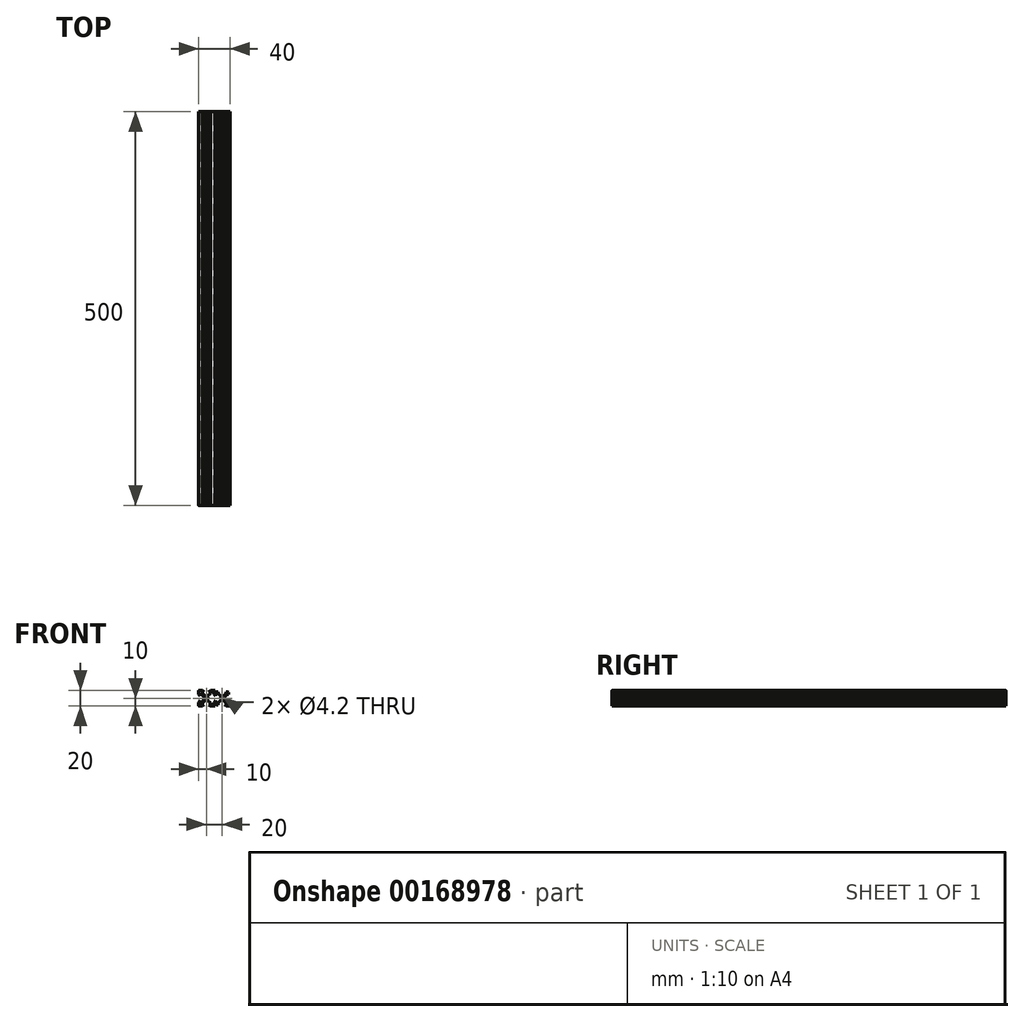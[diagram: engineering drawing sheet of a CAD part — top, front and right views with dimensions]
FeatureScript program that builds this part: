
annotation { "Feature Type Name" : "Feature", "Feature Type Description" : "" }
export const myFeature = defineFeature(function(context is Context, id is Id, definition is map)
    precondition{}
    {
        {
            var Q0;
            Q0=qCreatedBy(makeId("Front.planeOp"),FACE);
            var sketch = newSketch(context, id + "F0", { "sketchPlane" : qUnion([Q0])});
            skLineSegment(sketch, "E0.left", {"start": v(15, 1) * mm, "end": v(15, 4.89) * mm});
            skLineSegment(sketch, "E0.right", {"start": v(35, 1) * mm, "end": v(35, 4.89) * mm});
            skLineSegment(sketch, "E1.right", {"start": v(33.2, 2.97) * mm, "end": v(33.2, 7.06) * mm});
            skLineSegment(sketch, "E2.rect.bottom", {"start": v(26.78, 12.84) * mm, "end": v(23.22, 12.84) * mm});
            skLineSegment(sketch, "E2.rect.top", {"start": v(26.78, 7.16) * mm, "end": v(23.31, 7.16) * mm});
            skLineSegment(sketch, "E2.rect.left", {"start": v(27.84, 11.78) * mm, "end": v(27.84, 8.33) * mm});
            skLineSegment(sketch, "E2.rect.right", {"start": v(22.16, 11.78) * mm, "end": v(22.16, 8.22) * mm});
            skLineSegment(sketch, "E3.rect.bottom", {"start": v(35, 15.12) * mm, "end": v(35, 15.12) * mm});
            skLineSegment(sketch, "E4.rect.bottom", {"start": v(33.2, 12.95) * mm, "end": v(33.2, 12.95) * mm});
            skPoint(sketch, "E4.rect.middle", {"position": v(33.2, 10) * mm});
            skLineSegment(sketch, "E5", {"start": v(35, 4.88) * mm, "end": v(33.2, 7.05) * mm});
            skLineSegment(sketch, "E6", {"start": v(28.37, 12.3) * mm, "end": v(33.2, 17.14) * mm});
            skLineSegment(sketch, "E7", {"start": v(27.3, 13.37) * mm, "end": v(32.14, 18.2) * mm});
            skLineSegment(sketch, "E8", {"start": v(22.7, 13.37) * mm, "end": v(17.86, 18.2) * mm});
            skLineSegment(sketch, "E9", {"start": v(28.37, 7.8) * mm, "end": v(33.2, 2.97) * mm});
            skLineSegment(sketch, "E10", {"start": v(22.74, 6.58) * mm, "end": v(17.95, 1.8) * mm});
            skLineSegment(sketch, "E11", {"start": v(27.36, 6.58) * mm, "end": v(32.14, 1.8) * mm});
            skLineSegment(sketch, "E12", {"start": v(21.63, 7.7) * mm, "end": v(16.8, 2.86) * mm});
            skLineSegment(sketch, "E13", {"start": v(22.7, 13.37) * mm, "end": v(23.22, 12.84) * mm});
            skLineSegment(sketch, "E14", {"start": v(27.3, 13.37) * mm, "end": v(26.78, 12.84) * mm});
            skLineSegment(sketch, "E15", {"start": v(28.37, 12.3) * mm, "end": v(27.84, 11.78) * mm});
            skLineSegment(sketch, "E16", {"start": v(28.37, 7.8) * mm, "end": v(27.84, 8.33) * mm});
            skLineSegment(sketch, "E17", {"start": v(27.36, 6.58) * mm, "end": v(26.78, 7.16) * mm});
            skLineSegment(sketch, "E18", {"start": v(22.74, 6.58) * mm, "end": v(23.31, 7.16) * mm});
            skLineSegment(sketch, "E19", {"start": v(21.63, 7.7) * mm, "end": v(22.16, 8.22) * mm});
            skLineSegment(sketch, "E20", {"start": v(21.63, 12.3) * mm, "end": v(16.8, 17.14) * mm});
            skLineSegment(sketch, "E21", {"start": v(21.63, 12.3) * mm, "end": v(22.16, 11.78) * mm});
            skPoint(sketch, "E22.orphan", {"position": v(22.16, 12.84) * mm});
            skPoint(sketch, "E23.orphan", {"position": v(27.84, 12.84) * mm});
            skPoint(sketch, "E24.orphan", {"position": v(27.84, 7.16) * mm});
            skPoint(sketch, "E25.orphan", {"position": v(22.16, 7.16) * mm});
            skPoint(sketch, "E26.orphan", {"position": v(33.2, 18.2) * mm});
            skPoint(sketch, "E27.orphan", {"position": v(33.2, 1.8) * mm});
            skLineSegment(sketch, "E28.trimOffspring", {"start": v(35, 15.12) * mm, "end": v(35, 19) * mm});
            skLineSegment(sketch, "E29.rect.left", {"start": v(28.21, 18.2) * mm, "end": v(28.21, 18.2) * mm});
            skLineSegment(sketch, "E29.rect.right", {"start": v(21.79, 18.2) * mm, "end": v(21.79, 18.2) * mm});
            skLineSegment(sketch, "E30.rect.left", {"start": v(27.72, 16.15) * mm, "end": v(27.72, 16.15) * mm});
            skLineSegment(sketch, "E30.rect.right", {"start": v(21.83, 16.15) * mm, "end": v(21.83, 16.15) * mm});
            skLineSegment(sketch, "E31.trimOffspring", {"start": v(15, 15.12) * mm, "end": v(15, 19) * mm});
            skPoint(sketch, "E32.visualSharp", {"position": v(15, 20) * mm});
            skArc(sketch, "E32.filletArc", {"start": v(16, 20) * mm, "mid": v(15.3, 19.7) * mm, "end": v(15, 19) * mm});
            skArc(sketch, "E33.filletArc", {"start": v(34, 0) * mm, "mid": v(34.7, 0.3) * mm, "end": v(35, 1) * mm});
            skPoint(sketch, "E34.visualSharp", {"position": v(35, 20) * mm});
            skArc(sketch, "E34.filletArc", {"start": v(35, 19) * mm, "mid": v(34.7, 19.7) * mm, "end": v(34, 20) * mm});
            skLineSegment(sketch, "E35", {"start": v(17.95, 1.8) * mm, "end": v(17.95, 0) * mm});
            skArc(sketch, "E36.filletArc", {"start": v(15, 1) * mm, "mid": v(15.3, 0.3) * mm, "end": v(16, 0) * mm});
            skLineSegment(sketch, "E37", {"start": v(16.8, 17.14) * mm, "end": v(17.86, 18.2) * mm});
            skPoint(sketch, "E38.visualSharp", {"position": v(16.8, 12.95) * mm});
            skLineSegment(sketch, "E39", {"start": v(16.8, 2.86) * mm, "end": v(17.95, 1.8) * mm});
            skLineSegment(sketch, "E40", {"start": v(32.14, 1.8) * mm, "end": v(33.2, 2.97) * mm});
            skLineSegment(sketch, "E41", {"start": v(32.14, 18.2) * mm, "end": v(33.2, 17.14) * mm});
            skLineSegment(sketch, "E42", {"start": v(33.2, 17.14) * mm, "end": v(33.2, 12.94) * mm});
            skLineSegment(sketch, "E43", {"start": v(35, 15.12) * mm, "end": v(33.2, 12.95) * mm});
            skPoint(sketch, "E44.visualSharp", {"position": v(16.8, 7.06) * mm});
            skLineSegment(sketch, "E45", {"start": v(33.2, 15.12) * mm, "end": v(31.18, 15.12) * mm});
            skLineSegment(sketch, "E46", {"start": v(16.8, 15.12) * mm, "end": v(18.82, 15.12) * mm});
            skLineSegment(sketch, "E47", {"start": v(16.8, 4.89) * mm, "end": v(18.82, 4.89) * mm});
            skLineSegment(sketch, "E48", {"start": v(33.2, 4.89) * mm, "end": v(31.28, 4.88) * mm});
            skLineSegment(sketch, "E49.rect.left", {"start": v(26.7, 18.2) * mm, "end": v(26.7, 18.2) * mm});
            skLineSegment(sketch, "E49.rect.right", {"start": v(23.3, 18.2) * mm, "end": v(23.3, 18.2) * mm});
            skPoint(sketch, "E49.rect.middle", {"position": v(25, 18.2) * mm});
            skLineSegment(sketch, "E50.rect.left", {"start": v(30.11, 20) * mm, "end": v(30.11, 20) * mm});
            skLineSegment(sketch, "E50.rect.right", {"start": v(19.88, 20) * mm, "end": v(19.88, 20) * mm});
            skPoint(sketch, "E50.rect.middle", {"position": v(25, 20) * mm});
            skLineSegment(sketch, "E51.rect.left", {"start": v(27.95, 18.2) * mm, "end": v(27.95, 18.2) * mm});
            skLineSegment(sketch, "E51.rect.right", {"start": v(22.05, 18.2) * mm, "end": v(22.05, 18.2) * mm});
            skLineSegment(sketch, "E52", {"start": v(22.05, 18.2) * mm, "end": v(19.88, 20) * mm});
            skLineSegment(sketch, "E53", {"start": v(27.94, 18.2) * mm, "end": v(30.11, 20) * mm});
            skLineSegment(sketch, "E54", {"start": v(27.94, 18.2) * mm, "end": v(32.14, 18.2) * mm});
            skLineSegment(sketch, "E55", {"start": v(30.11, 20) * mm, "end": v(34, 20) * mm});
            skLineSegment(sketch, "E56", {"start": v(19.88, 20) * mm, "end": v(16, 20) * mm});
            skLineSegment(sketch, "E57", {"start": v(17.86, 18.2) * mm, "end": v(22.05, 18.2) * mm});
            skLineSegment(sketch, "E58", {"start": v(15, 15.11) * mm, "end": v(16.8, 12.94) * mm});
            skLineSegment(sketch, "E59", {"start": v(16.8, 17.14) * mm, "end": v(16.8, 12.95) * mm});
            skLineSegment(sketch, "E60", {"start": v(15, 4.89) * mm, "end": v(16.8, 7.06) * mm});
            skLineSegment(sketch, "E61", {"start": v(16.8, 2.86) * mm, "end": v(16.8, 7.06) * mm});
            skLineSegment(sketch, "E62", {"start": v(22.05, 1.8) * mm, "end": v(19.88, 0) * mm});
            skLineSegment(sketch, "E63", {"start": v(27.94, 1.8) * mm, "end": v(30.11, 0) * mm});
            skLineSegment(sketch, "E64", {"start": v(16, 0) * mm, "end": v(19.88, 0) * mm});
            skLineSegment(sketch, "E65", {"start": v(30.11, 0) * mm, "end": v(34, 0) * mm});
            skLineSegment(sketch, "E66", {"start": v(27.94, 1.8) * mm, "end": v(32.14, 1.8) * mm});
            skLineSegment(sketch, "E67", {"start": v(22.05, 1.8) * mm, "end": v(17.95, 1.8) * mm});
            skLineSegment(sketch, "E68", {"start": v(19.88, 1.8) * mm, "end": v(19.88, 3.73) * mm});
            skLineSegment(sketch, "E69", {"start": v(30.11, 1.8) * mm, "end": v(30.11, 3.83) * mm});
            skLineSegment(sketch, "E70", {"start": v(30.11, 18.2) * mm, "end": v(30.11, 16.18) * mm});
            skLineSegment(sketch, "E71", {"start": v(19.88, 16.18) * mm, "end": v(19.88, 18.2) * mm});
            skLineSegment(sketch, "E72", {"start": v(15, 0) * mm, "end": v(-35, 0) * mm});
            skLineSegment(sketch, "E73", {"start": v(35, 0) * mm, "end": v(35, 20) * mm});
            skLineSegment(sketch, "E74", {"start": v(34, 0) * mm, "end": v(35, 0) * mm});
            skLineSegment(sketch, "E75", {"start": v(34, 20) * mm, "end": v(35, 20) * mm});
            skLineSegment(sketch, "E76.0.MirrorCS", {"start": v(36, 0) * mm, "end": v(35, 0) * mm});
            skArc(sketch, "E76.1.MirrorCS", {"start": v(36, 0) * mm, "mid": v(35.3, 0.3) * mm, "end": v(35, 1) * mm});
            skLineSegment(sketch, "E76.2.MirrorCS", {"start": v(36, 20) * mm, "end": v(35, 20) * mm});
            skLineSegment(sketch, "E76.3.MirrorCS", {"start": v(54, 0) * mm, "end": v(50.12, 0) * mm});
            skLineSegment(sketch, "E76.4.MirrorCS", {"start": v(48.37, 7.7) * mm, "end": v(47.84, 8.22) * mm});
            skArc(sketch, "E76.5.MirrorCS", {"start": v(35, 19) * mm, "mid": v(35.3, 19.7) * mm, "end": v(36, 20) * mm});
            skLineSegment(sketch, "E76.6.MirrorCS", {"start": v(37.86, 1.8) * mm, "end": v(36.8, 2.97) * mm});
            skArc(sketch, "E76.7.MirrorCS", {"start": v(54, 20) * mm, "mid": v(54.7, 19.7) * mm, "end": v(55, 19) * mm});
            skLineSegment(sketch, "E76.8.MirrorCS", {"start": v(42.64, 6.58) * mm, "end": v(43.22, 7.16) * mm});
            skLineSegment(sketch, "E76.9.MirrorCS", {"start": v(41.63, 7.8) * mm, "end": v(42.16, 8.33) * mm});
            skLineSegment(sketch, "E76.10.MirrorCS", {"start": v(37.86, 18.2) * mm, "end": v(36.8, 17.14) * mm});
            skLineSegment(sketch, "E76.11.MirrorCS", {"start": v(42.7, 13.37) * mm, "end": v(43.22, 12.84) * mm});
            skLineSegment(sketch, "E76.12.MirrorCS", {"start": v(53.2, 2.86) * mm, "end": v(52.05, 1.8) * mm});
            skLineSegment(sketch, "E76.13.MirrorCS", {"start": v(53.2, 17.14) * mm, "end": v(52.14, 18.2) * mm});
            skLineSegment(sketch, "E76.14.MirrorCS", {"start": v(48.37, 12.3) * mm, "end": v(47.84, 11.78) * mm});
            skLineSegment(sketch, "E76.15.MirrorCS", {"start": v(47.3, 13.37) * mm, "end": v(46.78, 12.84) * mm});
            skLineSegment(sketch, "E76.16.MirrorCS", {"start": v(47.26, 6.58) * mm, "end": v(46.69, 7.16) * mm});
            skLineSegment(sketch, "E76.17.MirrorCS", {"start": v(36.8, 15.12) * mm, "end": v(38.82, 15.12) * mm});
            skLineSegment(sketch, "E76.19.MirrorCS", {"start": v(54, 0) * mm, "end": v(50.12, 0) * mm});
            skLineSegment(sketch, "E76.20.MirrorCS", {"start": v(36.8, 4.89) * mm, "end": v(38.72, 4.88) * mm});
            skArc(sketch, "E76.21.MirrorCS", {"start": v(55, 1) * mm, "mid": v(54.7, 0.3) * mm, "end": v(54, 0) * mm});
            skLineSegment(sketch, "E76.22.MirrorCS", {"start": v(55, 4.89) * mm, "end": v(53.2, 7.06) * mm});
            skLineSegment(sketch, "E76.23.MirrorCS", {"start": v(52.14, 18.2) * mm, "end": v(47.95, 18.2) * mm});
            skLineSegment(sketch, "E76.25.MirrorCS", {"start": v(47.95, 18.2) * mm, "end": v(50.12, 20) * mm});
            skLineSegment(sketch, "E76.26.MirrorCS", {"start": v(50.12, 1.8) * mm, "end": v(50.12, 3.73) * mm});
            skLineSegment(sketch, "E76.27.MirrorCS", {"start": v(39.89, 0) * mm, "end": v(36, 0) * mm});
            skLineSegment(sketch, "E76.28.MirrorCS", {"start": v(53.2, 15.12) * mm, "end": v(51.18, 15.12) * mm});
            skPoint(sketch, "E76.29.MirrorP", {"position": v(45, 18.2) * mm});
            skLineSegment(sketch, "E76.30.MirrorCS", {"start": v(48.21, 18.2) * mm, "end": v(48.21, 18.2) * mm});
            skLineSegment(sketch, "E76.31.MirrorCS", {"start": v(42.06, 18.2) * mm, "end": v(39.89, 20) * mm});
            skLineSegment(sketch, "E76.32.MirrorCS", {"start": v(41.63, 12.3) * mm, "end": v(42.16, 11.78) * mm});
            skLineSegment(sketch, "E76.33.MirrorCS", {"start": v(41.79, 18.2) * mm, "end": v(41.79, 18.2) * mm});
            skLineSegment(sketch, "E76.34.MirrorCS", {"start": v(36.8, 17.14) * mm, "end": v(36.8, 12.94) * mm});
            skLineSegment(sketch, "E76.35.MirrorCS", {"start": v(50.12, 16.18) * mm, "end": v(50.12, 18.2) * mm});
            skLineSegment(sketch, "E76.36.MirrorCS", {"start": v(42.06, 1.8) * mm, "end": v(39.89, 0) * mm});
            skLineSegment(sketch, "E76.37.MirrorCS", {"start": v(35, 15.12) * mm, "end": v(36.8, 12.95) * mm});
            skLineSegment(sketch, "E76.38.MirrorCS", {"start": v(35, 4.88) * mm, "end": v(36.8, 7.05) * mm});
            skLineSegment(sketch, "E76.39.MirrorCS", {"start": v(53.2, 17.14) * mm, "end": v(53.2, 12.95) * mm});
            skLineSegment(sketch, "E76.40.MirrorCS", {"start": v(55, 15.12) * mm, "end": v(53.2, 12.94) * mm});
            skLineSegment(sketch, "E76.41.MirrorCS", {"start": v(53.2, 4.89) * mm, "end": v(51.18, 4.89) * mm});
            skLineSegment(sketch, "E76.42.MirrorCS", {"start": v(36.8, 2.97) * mm, "end": v(36.8, 7.06) * mm});
            skLineSegment(sketch, "E76.43.MirrorCS", {"start": v(39.89, 18.2) * mm, "end": v(39.89, 16.18) * mm});
            skLineSegment(sketch, "E76.44.MirrorCS", {"start": v(42.06, 18.2) * mm, "end": v(37.86, 18.2) * mm});
            skLineSegment(sketch, "E76.45.MirrorCS", {"start": v(53.2, 2.86) * mm, "end": v(53.2, 7.06) * mm});
            skLineSegment(sketch, "E76.46.MirrorCS", {"start": v(42.06, 1.8) * mm, "end": v(37.86, 1.8) * mm});
            skLineSegment(sketch, "E76.47.MirrorCS", {"start": v(52.05, 1.8) * mm, "end": v(52.05, 0) * mm});
            skLineSegment(sketch, "E76.48.MirrorCS", {"start": v(39.89, 1.8) * mm, "end": v(39.89, 3.83) * mm});
            skPoint(sketch, "E76.49.MirrorP", {"position": v(55, 20) * mm});
            skLineSegment(sketch, "E76.50.MirrorCS", {"start": v(47.95, 1.8) * mm, "end": v(52.05, 1.8) * mm});
            skLineSegment(sketch, "E76.51.MirrorCS", {"start": v(41.63, 7.8) * mm, "end": v(36.8, 2.97) * mm});
            skPoint(sketch, "E76.52.MirrorP", {"position": v(53.2, 7.06) * mm});
            skLineSegment(sketch, "E76.53.MirrorCS", {"start": v(43.22, 7.16) * mm, "end": v(46.69, 7.16) * mm});
            skLineSegment(sketch, "E76.54.MirrorCS", {"start": v(55, 1) * mm, "end": v(55, 4.89) * mm});
            skLineSegment(sketch, "E76.55.MirrorCS", {"start": v(55, 15.12) * mm, "end": v(55, 19) * mm});
            skLineSegment(sketch, "E76.56.MirrorCS", {"start": v(48.37, 12.3) * mm, "end": v(53.2, 17.14) * mm});
            skLineSegment(sketch, "E76.57.MirrorCS", {"start": v(42.28, 16.15) * mm, "end": v(42.28, 16.15) * mm});
            skLineSegment(sketch, "E76.58.MirrorCS", {"start": v(36.8, 12.95) * mm, "end": v(36.8, 12.95) * mm});
            skLineSegment(sketch, "E76.60.MirrorCS", {"start": v(42.05, 18.2) * mm, "end": v(42.05, 18.2) * mm});
            skLineSegment(sketch, "E76.61.MirrorCS", {"start": v(47.26, 6.58) * mm, "end": v(52.05, 1.8) * mm});
            skLineSegment(sketch, "E76.62.MirrorCS", {"start": v(42.7, 13.37) * mm, "end": v(37.86, 18.2) * mm});
            skPoint(sketch, "E76.63.MirrorP", {"position": v(42.16, 12.84) * mm});
            skLineSegment(sketch, "E76.64.MirrorCS", {"start": v(48.17, 16.15) * mm, "end": v(48.17, 16.15) * mm});
            skLineSegment(sketch, "E76.65.MirrorCS", {"start": v(42.16, 11.78) * mm, "end": v(42.16, 8.33) * mm});
            skLineSegment(sketch, "E76.66.MirrorCS", {"start": v(47.84, 11.78) * mm, "end": v(47.84, 8.22) * mm});
            skLineSegment(sketch, "E76.67.MirrorCS", {"start": v(43.22, 12.84) * mm, "end": v(46.78, 12.84) * mm});
            skPoint(sketch, "E76.68.MirrorP", {"position": v(36.8, 18.2) * mm});
            skPoint(sketch, "E76.69.MirrorP", {"position": v(53.2, 12.95) * mm});
            skLineSegment(sketch, "E76.72.MirrorCS", {"start": v(39.89, 20) * mm, "end": v(36, 20) * mm});
            skPoint(sketch, "E76.73.MirrorP", {"position": v(42.16, 7.16) * mm});
            skLineSegment(sketch, "E76.74.MirrorCS", {"start": v(47.3, 13.37) * mm, "end": v(52.14, 18.2) * mm});
            skLineSegment(sketch, "E76.75.MirrorCS", {"start": v(43.3, 18.2) * mm, "end": v(43.3, 18.2) * mm});
            skLineSegment(sketch, "E76.76.MirrorCS", {"start": v(39.89, 0) * mm, "end": v(36, 0) * mm});
            skLineSegment(sketch, "E76.77.MirrorCS", {"start": v(54, 0) * mm, "end": v(50.12, 0) * mm});
            skLineSegment(sketch, "E76.78.MirrorCS", {"start": v(39.89, 0) * mm, "end": v(36, 0) * mm});
            skPoint(sketch, "E76.79.MirrorP", {"position": v(45, 20) * mm});
            skPoint(sketch, "E76.80.MirrorP", {"position": v(47.84, 7.16) * mm});
            skLineSegment(sketch, "E76.81.MirrorCS", {"start": v(39.89, 20) * mm, "end": v(39.89, 20) * mm});
            skLineSegment(sketch, "E76.82.MirrorCS", {"start": v(47.95, 18.2) * mm, "end": v(47.95, 18.2) * mm});
            skLineSegment(sketch, "E76.83.MirrorCS", {"start": v(50.12, 20) * mm, "end": v(50.12, 20) * mm});
            skLineSegment(sketch, "E76.84.MirrorCS", {"start": v(41.63, 12.3) * mm, "end": v(36.8, 17.14) * mm});
            skLineSegment(sketch, "E76.85.MirrorCS", {"start": v(48.37, 7.7) * mm, "end": v(53.2, 2.86) * mm});
            skPoint(sketch, "E76.86.MirrorP", {"position": v(36.8, 1.8) * mm});
            skPoint(sketch, "E76.87.MirrorP", {"position": v(36.8, 10) * mm});
            skPoint(sketch, "E76.88.MirrorP", {"position": v(45, 18.2) * mm});
            skPoint(sketch, "E76.89.MirrorP", {"position": v(47.84, 12.84) * mm});
            skLineSegment(sketch, "E76.90.MirrorCS", {"start": v(47.95, 1.8) * mm, "end": v(50.12, 0) * mm});
            skLineSegment(sketch, "E76.91.MirrorCS", {"start": v(42.64, 6.58) * mm, "end": v(37.86, 1.8) * mm});
            skLineSegment(sketch, "E76.94.MirrorCS", {"start": v(50.12, 20) * mm, "end": v(54, 20) * mm});
            skLineSegment(sketch, "E76.95.MirrorCS", {"start": v(46.7, 18.2) * mm, "end": v(46.7, 18.2) * mm});
            skSolve(sketch);
        }
        {
            var Q0;
            {var subQ1=sQuery(id+"F0.wireOp",EDGE,"E76.41.MirrorCS");Q0=makeQuery(id+"F0.imprint","IMPRINT",FACE,{"disambiguationData":[TD([[makeQuery(id+"F0.imprint","IMPRINT",EDGE,{"derivedFrom":subQ1}),1.0]])]});}
            var Q1;
            Q1=makeQuery(id+"F0.imprint","IMPRINT",FACE,{"disambiguationData":[TD([[makeQuery(id+"F0.imprint","IMPRINT",EDGE,{"derivedFrom":sQuery(id+"F0.wireOp",EDGE,"E76.1.MirrorCS")}),-1.0]])]});
            var Q2;
            {var subQ4=sQuery(id+"F0.wireOp",EDGE,"E5");Q2=makeQuery(id+"F0.imprint","IMPRINT",FACE,{"disambiguationData":[TD([[makeQuery(id+"F0.imprint","IMPRINT",EDGE,{"derivedFrom":subQ4}),1.0]])]});}
            var Q3;
            Q3=makeQuery(id+"F0.imprint","IMPRINT",FACE,{"disambiguationData":[TD([[makeQuery(id+"F0.imprint","IMPRINT",EDGE,{"derivedFrom":sQuery(id+"F0.wireOp",EDGE,"E0.left")}),-1.0]])]});
            var Q4;
            {var subQ6=sQuery(id+"F0.wireOp",EDGE,"E76.12.MirrorCS");Q4=makeQuery(id+"F0.imprint","IMPRINT",FACE,{"disambiguationData":[TD([[makeQuery(id+"F0.imprint","IMPRINT",EDGE,{"derivedFrom":subQ6}),1.0]])]});}
            var Q5;
            {var subQ2=sQuery(id+"F0.wireOp",EDGE,"E76.47.MirrorCS");Q5=makeQuery(id+"F0.imprint","IMPRINT",FACE,{"disambiguationData":[TD([[makeQuery(id+"F0.imprint","IMPRINT",EDGE,{"derivedFrom":subQ2}),-1.0]])]});}
            var Q6;
            {var subQ6=sQuery(id+"F0.wireOp",EDGE,"E76.4.MirrorCS");Q6=makeQuery(id+"F0.imprint","IMPRINT",FACE,{"disambiguationData":[TD([[makeQuery(id+"F0.imprint","IMPRINT",EDGE,{"derivedFrom":subQ6}),1.0]])]});}
            var Q7;
            {var subQ2=sQuery(id+"F0.wireOp",EDGE,"E35");Q7=makeQuery(id+"F0.imprint","IMPRINT",FACE,{"disambiguationData":[TD([[makeQuery(id+"F0.imprint","IMPRINT",EDGE,{"derivedFrom":subQ2}),1.0]])]});}
            var Q8;
            Q8=makeQuery(id+"F0.imprint","IMPRINT",FACE,{"disambiguationData":[TD([[makeQuery(id+"F0.imprint","IMPRINT",EDGE,{"derivedFrom":sQuery(id+"F0.wireOp",EDGE,"E76.5.MirrorCS")}),-1.0]])]});
            var Q9;
            Q9=makeQuery(id+"F0.imprint","IMPRINT",FACE,{"disambiguationData":[TD([[makeQuery(id+"F0.imprint","IMPRINT",EDGE,{"derivedFrom":sQuery(id+"F0.wireOp",EDGE,"E31.trimOffspring")}),-1.0]])]});
            var Q10;
            {var subQ1=sQuery(id+"F0.wireOp",EDGE,"E76.17.MirrorCS");Q10=makeQuery(id+"F0.imprint","IMPRINT",FACE,{"disambiguationData":[TD([[makeQuery(id+"F0.imprint","IMPRINT",EDGE,{"derivedFrom":subQ1}),1.0]])]});}
            var Q11;
            {var subQ1=sQuery(id+"F0.wireOp",EDGE,"E76.35.MirrorCS");Q11=makeQuery(id+"F0.imprint","IMPRINT",FACE,{"disambiguationData":[TD([[makeQuery(id+"F0.imprint","IMPRINT",EDGE,{"derivedFrom":subQ1}),-1.0]])]});}
            var Q12;
            Q12=makeQuery(id+"F0.imprint","IMPRINT",FACE,{"disambiguationData":[TD([[makeQuery(id+"F0.imprint","IMPRINT",EDGE,{"derivedFrom":sQuery(id+"F0.wireOp",EDGE,"E34.filletArc")}),1.0]])]});
            var Q13;
            {var subQ5=sQuery(id+"F0.wireOp",EDGE,"E76.9.MirrorCS");Q13=makeQuery(id+"F0.imprint","IMPRINT",FACE,{"disambiguationData":[TD([[makeQuery(id+"F0.imprint","IMPRINT",EDGE,{"derivedFrom":subQ5}),1.0]])]});}
            var Q14;
            Q14=makeQuery(id+"F0.imprint","IMPRINT",FACE,{"disambiguationData":[TD([[makeQuery(id+"F0.imprint","IMPRINT",EDGE,{"derivedFrom":sQuery(id+"F0.wireOp",EDGE,"E76.7.MirrorCS")}),-1.0]])]});
            var Q15;
            Q15=makeQuery(id+"F0.imprint","IMPRINT",FACE,{"disambiguationData":[TD([[makeQuery(id+"F0.imprint","IMPRINT",EDGE,{"derivedFrom":sQuery(id+"F0.wireOp",EDGE,"E2.rect.bottom")}),1.0]])]});
            var Q16;
            {var subQ0=sQuery(id+"F0.wireOp",EDGE,"E70");Q16=makeQuery(id+"F0.imprint","IMPRINT",FACE,{"disambiguationData":[TD([[makeQuery(id+"F0.imprint","IMPRINT",EDGE,{"derivedFrom":subQ0}),1.0]])]});}
            var Q17;
            {var subQ1=sQuery(id+"F0.wireOp",EDGE,"E76.28.MirrorCS");Q17=makeQuery(id+"F0.imprint","IMPRINT",FACE,{"disambiguationData":[TD([[makeQuery(id+"F0.imprint","IMPRINT",EDGE,{"derivedFrom":subQ1}),-1.0]])]});}
            var Q18;
            Q18=makeQuery(id+"F0.imprint","IMPRINT",FACE,{"disambiguationData":[TD([[makeQuery(id+"F0.imprint","IMPRINT",EDGE,{"derivedFrom":sQuery(id+"F0.wireOp",EDGE,"E2.rect.left")}),1.0]])]});
            var Q19;
            {var subQ1=sQuery(id+"F0.wireOp",EDGE,"E71");Q19=makeQuery(id+"F0.imprint","IMPRINT",FACE,{"disambiguationData":[TD([[makeQuery(id+"F0.imprint","IMPRINT",EDGE,{"derivedFrom":subQ1}),1.0]])]});}
            var Q20;
            {var subQ1=sQuery(id+"F0.wireOp",EDGE,"E47");Q20=makeQuery(id+"F0.imprint","IMPRINT",FACE,{"disambiguationData":[TD([[makeQuery(id+"F0.imprint","IMPRINT",EDGE,{"derivedFrom":subQ1}),-1.0]])]});}
            var Q21;
            {var subQ0=sQuery(id+"F0.wireOp",EDGE,"E69");Q21=makeQuery(id+"F0.imprint","IMPRINT",FACE,{"disambiguationData":[TD([[makeQuery(id+"F0.imprint","IMPRINT",EDGE,{"derivedFrom":subQ0}),-1.0]])]});}
            var Q22;
            {var subQ1=sQuery(id+"F0.wireOp",EDGE,"E76.48.MirrorCS");Q22=makeQuery(id+"F0.imprint","IMPRINT",FACE,{"disambiguationData":[TD([[makeQuery(id+"F0.imprint","IMPRINT",EDGE,{"derivedFrom":subQ1}),1.0]])]});}
            var Q23;
            {var subQ1=sQuery(id+"F0.wireOp",EDGE,"E46");Q23=makeQuery(id+"F0.imprint","IMPRINT",FACE,{"disambiguationData":[TD([[makeQuery(id+"F0.imprint","IMPRINT",EDGE,{"derivedFrom":subQ1}),1.0]])]});}
            var Q24;
            {var subQ1=sQuery(id+"F0.wireOp",EDGE,"E76.26.MirrorCS");Q24=makeQuery(id+"F0.imprint","IMPRINT",FACE,{"disambiguationData":[TD([[makeQuery(id+"F0.imprint","IMPRINT",EDGE,{"derivedFrom":subQ1}),-1.0]])]});}
            var Q25;
            {var subQ1=sQuery(id+"F0.wireOp",EDGE,"E76.43.MirrorCS");Q25=makeQuery(id+"F0.imprint","IMPRINT",FACE,{"disambiguationData":[TD([[makeQuery(id+"F0.imprint","IMPRINT",EDGE,{"derivedFrom":subQ1}),-1.0]])]});}
            var Q26;
            {var subQ0=sQuery(id+"F0.wireOp",EDGE,"E48");Q26=makeQuery(id+"F0.imprint","IMPRINT",FACE,{"disambiguationData":[TD([[makeQuery(id+"F0.imprint","IMPRINT",EDGE,{"derivedFrom":subQ0}),1.0]])]});}
            var Q27;
            {var subQ0=sQuery(id+"F0.wireOp",EDGE,"E45");Q27=makeQuery(id+"F0.imprint","IMPRINT",FACE,{"disambiguationData":[TD([[makeQuery(id+"F0.imprint","IMPRINT",EDGE,{"derivedFrom":subQ0}),-1.0]])]});}
            var Q28;
            {var subQ1=sQuery(id+"F0.wireOp",EDGE,"E76.20.MirrorCS");Q28=makeQuery(id+"F0.imprint","IMPRINT",FACE,{"disambiguationData":[TD([[makeQuery(id+"F0.imprint","IMPRINT",EDGE,{"derivedFrom":subQ1}),-1.0]])]});}
            var Q29;
            {var subQ0=sQuery(id+"F0.wireOp",EDGE,"E68");Q29=makeQuery(id+"F0.imprint","IMPRINT",FACE,{"disambiguationData":[TD([[makeQuery(id+"F0.imprint","IMPRINT",EDGE,{"derivedFrom":subQ0}),1.0]])]});}
            var Q30;
            {var subQ1=sQuery(id+"F0.wireOp",EDGE,"E76.2.MirrorCS");Q30=makeQuery(id+"F0.imprint","IMPRINT",FACE,{"disambiguationData":[TD([[makeQuery(id+"F0.imprint","IMPRINT",EDGE,{"derivedFrom":subQ1}),1.0]])]});}
            var Q31;
            {var subQ2=sQuery(id+"F0.wireOp",EDGE,"E34.filletArc");Q31=makeQuery(id+"F0.imprint","IMPRINT",FACE,{"disambiguationData":[TD([[makeQuery(id+"F0.imprint","IMPRINT",EDGE,{"derivedFrom":subQ2}),-1.0]])]});}
            var Q32;
            {var subQ1=sQuery(id+"F0.wireOp",EDGE,"E76.0.MirrorCS");Q32=makeQuery(id+"F0.imprint","IMPRINT",FACE,{"disambiguationData":[TD([[makeQuery(id+"F0.imprint","IMPRINT",EDGE,{"derivedFrom":subQ1}),-1.0]])]});}
            var Q33;
            {var subQ2=sQuery(id+"F0.wireOp",EDGE,"E33.filletArc");Q33=makeQuery(id+"F0.imprint","IMPRINT",FACE,{"disambiguationData":[TD([[makeQuery(id+"F0.imprint","IMPRINT",EDGE,{"derivedFrom":subQ2}),-1.0]])]});}
            extrude(context, id + "F1", {"entities" : qUnion([Q0, Q1, Q2, Q3, Q4, Q5, Q6, Q7, Q8, Q9, Q10, Q11, Q12, Q13, Q14, Q15, Q16, Q17, Q18, Q19, Q20, Q21, Q22, Q23, Q24, Q25, Q26, Q27, Q28, Q29, Q30, Q31, Q32, Q33]), "depth" : 500 * mm});
        }
        {
            var Q0;
            Q0=makeQuery(id+"F1.opExtrude","CAP_FACE",FACE,{"disambiguationData":[OSD([sQuery(id+"F0.wireOp",EDGE,"E0.left"),sQuery(id+"F0.wireOp",EDGE,"E2.rect.bottom"),sQuery(id+"F0.wireOp",EDGE,"E2.rect.top"),sQuery(id+"F0.wireOp",EDGE,"E2.rect.right"),sQuery(id+"F0.wireOp",EDGE,"E7"),sQuery(id+"F0.wireOp",EDGE,"E8"),sQuery(id+"F0.wireOp",EDGE,"E10"),sQuery(id+"F0.wireOp",EDGE,"E11"),sQuery(id+"F0.wireOp",EDGE,"E12"),sQuery(id+"F0.wireOp",EDGE,"E13"),sQuery(id+"F0.wireOp",EDGE,"E14"),sQuery(id+"F0.wireOp",EDGE,"E17"),sQuery(id+"F0.wireOp",EDGE,"E18"),sQuery(id+"F0.wireOp",EDGE,"E19"),sQuery(id+"F0.wireOp",EDGE,"E20"),sQuery(id+"F0.wireOp",EDGE,"E21"),sQuery(id+"F0.wireOp",EDGE,"E31.trimOffspring"),sQuery(id+"F0.wireOp",EDGE,"E32.filletArc"),sQuery(id+"F0.wireOp",EDGE,"E36.filletArc"),sQuery(id+"F0.wireOp",EDGE,"E46"),sQuery(id+"F0.wireOp",EDGE,"E47"),sQuery(id+"F0.wireOp",EDGE,"E52"),sQuery(id+"F0.wireOp",EDGE,"E53"),sQuery(id+"F0.wireOp",EDGE,"E54"),sQuery(id+"F0.wireOp",EDGE,"E55"),sQuery(id+"F0.wireOp",EDGE,"E56"),sQuery(id+"F0.wireOp",EDGE,"E57"),sQuery(id+"F0.wireOp",EDGE,"E58"),sQuery(id+"F0.wireOp",EDGE,"E59"),sQuery(id+"F0.wireOp",EDGE,"E60"),sQuery(id+"F0.wireOp",EDGE,"E61"),sQuery(id+"F0.wireOp",EDGE,"E62"),sQuery(id+"F0.wireOp",EDGE,"E63"),sQuery(id+"F0.wireOp",EDGE,"E66"),sQuery(id+"F0.wireOp",EDGE,"E67"),sQuery(id+"F0.wireOp",EDGE,"E68"),sQuery(id+"F0.wireOp",EDGE,"E69"),sQuery(id+"F0.wireOp",EDGE,"E70"),sQuery(id+"F0.wireOp",EDGE,"E71"),sQuery(id+"F0.wireOp",EDGE,"E64"),sQuery(id+"F0.wireOp",EDGE,"E65"),sQuery(id+"F0.wireOp",EDGE,"E74"),sQuery(id+"F0.wireOp",EDGE,"E75"),sQuery(id+"F0.wireOp",EDGE,"E76.0.MirrorCS"),sQuery(id+"F0.wireOp",EDGE,"E76.2.MirrorCS"),sQuery(id+"F0.wireOp",EDGE,"E76.4.MirrorCS"),sQuery(id+"F0.wireOp",EDGE,"E76.7.MirrorCS"),sQuery(id+"F0.wireOp",EDGE,"E76.8.MirrorCS"),sQuery(id+"F0.wireOp",EDGE,"E76.11.MirrorCS"),sQuery(id+"F0.wireOp",EDGE,"E76.14.MirrorCS"),sQuery(id+"F0.wireOp",EDGE,"E76.15.MirrorCS"),sQuery(id+"F0.wireOp",EDGE,"E76.16.MirrorCS"),sQuery(id+"F0.wireOp",EDGE,"E76.21.MirrorCS"),sQuery(id+"F0.wireOp",EDGE,"E76.22.MirrorCS"),sQuery(id+"F0.wireOp",EDGE,"E76.23.MirrorCS"),sQuery(id+"F0.wireOp",EDGE,"E76.25.MirrorCS"),sQuery(id+"F0.wireOp",EDGE,"E76.26.MirrorCS"),sQuery(id+"F0.wireOp",EDGE,"E76.28.MirrorCS"),sQuery(id+"F0.wireOp",EDGE,"E76.31.MirrorCS"),sQuery(id+"F0.wireOp",EDGE,"E76.35.MirrorCS"),sQuery(id+"F0.wireOp",EDGE,"E76.36.MirrorCS"),sQuery(id+"F0.wireOp",EDGE,"E76.39.MirrorCS"),sQuery(id+"F0.wireOp",EDGE,"E76.40.MirrorCS"),sQuery(id+"F0.wireOp",EDGE,"E76.41.MirrorCS"),sQuery(id+"F0.wireOp",EDGE,"E76.43.MirrorCS"),sQuery(id+"F0.wireOp",EDGE,"E76.44.MirrorCS"),sQuery(id+"F0.wireOp",EDGE,"E76.45.MirrorCS"),sQuery(id+"F0.wireOp",EDGE,"E76.46.MirrorCS"),sQuery(id+"F0.wireOp",EDGE,"E76.48.MirrorCS"),sQuery(id+"F0.wireOp",EDGE,"E76.50.MirrorCS"),sQuery(id+"F0.wireOp",EDGE,"E76.53.MirrorCS"),sQuery(id+"F0.wireOp",EDGE,"E76.54.MirrorCS"),sQuery(id+"F0.wireOp",EDGE,"E76.55.MirrorCS"),sQuery(id+"F0.wireOp",EDGE,"E76.56.MirrorCS"),sQuery(id+"F0.wireOp",EDGE,"E76.61.MirrorCS"),sQuery(id+"F0.wireOp",EDGE,"E76.62.MirrorCS"),sQuery(id+"F0.wireOp",EDGE,"E76.66.MirrorCS"),sQuery(id+"F0.wireOp",EDGE,"E76.67.MirrorCS"),sQuery(id+"F0.wireOp",EDGE,"E76.72.MirrorCS"),sQuery(id+"F0.wireOp",EDGE,"E76.74.MirrorCS"),sQuery(id+"F0.wireOp",EDGE,"E76.77.MirrorCS"),sQuery(id+"F0.wireOp",EDGE,"E76.78.MirrorCS"),sQuery(id+"F0.wireOp",EDGE,"E76.85.MirrorCS"),sQuery(id+"F0.wireOp",EDGE,"E76.90.MirrorCS"),sQuery(id+"F0.wireOp",EDGE,"E76.91.MirrorCS"),sQuery(id+"F0.wireOp",EDGE,"E76.94.MirrorCS")])],"isStart":false});
            var sketch = newSketch(context, id + "F2", { "sketchPlane" : qUnion([Q0])});
            skPoint(sketch, "E77", {"position": v(45, 10) * mm});
            skPoint(sketch, "E77.positionSnap0", {"position": v(47.84, 10) * mm});
            skPoint(sketch, "E78", {"position": v(25, 10) * mm});
            skSolve(sketch);
        }
        {
            var Q0;
            Q0=sQuery(id+"F2.wireOp",VERTEX,"E77");
            var Q1;
            Q1=sQuery(id+"F2.wireOp",VERTEX,"E78");
            var Q2;
            Q2=makeQuery(id+"F1.opExtrude","SWEPT_BODY",BODY,{"disambiguationData":[OSD([sQuery(id+"F0.wireOp",EDGE,"E0.left"),sQuery(id+"F0.wireOp",EDGE,"E2.rect.bottom"),sQuery(id+"F0.wireOp",EDGE,"E2.rect.top"),sQuery(id+"F0.wireOp",EDGE,"E2.rect.right"),sQuery(id+"F0.wireOp",EDGE,"E7"),sQuery(id+"F0.wireOp",EDGE,"E8"),sQuery(id+"F0.wireOp",EDGE,"E10"),sQuery(id+"F0.wireOp",EDGE,"E11"),sQuery(id+"F0.wireOp",EDGE,"E12"),sQuery(id+"F0.wireOp",EDGE,"E13"),sQuery(id+"F0.wireOp",EDGE,"E14"),sQuery(id+"F0.wireOp",EDGE,"E17"),sQuery(id+"F0.wireOp",EDGE,"E18"),sQuery(id+"F0.wireOp",EDGE,"E19"),sQuery(id+"F0.wireOp",EDGE,"E20"),sQuery(id+"F0.wireOp",EDGE,"E21"),sQuery(id+"F0.wireOp",EDGE,"E31.trimOffspring"),sQuery(id+"F0.wireOp",EDGE,"E32.filletArc"),sQuery(id+"F0.wireOp",EDGE,"E36.filletArc"),sQuery(id+"F0.wireOp",EDGE,"E46"),sQuery(id+"F0.wireOp",EDGE,"E47"),sQuery(id+"F0.wireOp",EDGE,"E52"),sQuery(id+"F0.wireOp",EDGE,"E53"),sQuery(id+"F0.wireOp",EDGE,"E54"),sQuery(id+"F0.wireOp",EDGE,"E55"),sQuery(id+"F0.wireOp",EDGE,"E56"),sQuery(id+"F0.wireOp",EDGE,"E57"),sQuery(id+"F0.wireOp",EDGE,"E58"),sQuery(id+"F0.wireOp",EDGE,"E59"),sQuery(id+"F0.wireOp",EDGE,"E60"),sQuery(id+"F0.wireOp",EDGE,"E61"),sQuery(id+"F0.wireOp",EDGE,"E62"),sQuery(id+"F0.wireOp",EDGE,"E63"),sQuery(id+"F0.wireOp",EDGE,"E66"),sQuery(id+"F0.wireOp",EDGE,"E67"),sQuery(id+"F0.wireOp",EDGE,"E68"),sQuery(id+"F0.wireOp",EDGE,"E69"),sQuery(id+"F0.wireOp",EDGE,"E70"),sQuery(id+"F0.wireOp",EDGE,"E71"),sQuery(id+"F0.wireOp",EDGE,"E64"),sQuery(id+"F0.wireOp",EDGE,"E65"),sQuery(id+"F0.wireOp",EDGE,"E74"),sQuery(id+"F0.wireOp",EDGE,"E75"),sQuery(id+"F0.wireOp",EDGE,"E76.0.MirrorCS"),sQuery(id+"F0.wireOp",EDGE,"E76.2.MirrorCS"),sQuery(id+"F0.wireOp",EDGE,"E76.4.MirrorCS"),sQuery(id+"F0.wireOp",EDGE,"E76.7.MirrorCS"),sQuery(id+"F0.wireOp",EDGE,"E76.8.MirrorCS"),sQuery(id+"F0.wireOp",EDGE,"E76.11.MirrorCS"),sQuery(id+"F0.wireOp",EDGE,"E76.14.MirrorCS"),sQuery(id+"F0.wireOp",EDGE,"E76.15.MirrorCS"),sQuery(id+"F0.wireOp",EDGE,"E76.16.MirrorCS"),sQuery(id+"F0.wireOp",EDGE,"E76.21.MirrorCS"),sQuery(id+"F0.wireOp",EDGE,"E76.22.MirrorCS"),sQuery(id+"F0.wireOp",EDGE,"E76.23.MirrorCS"),sQuery(id+"F0.wireOp",EDGE,"E76.25.MirrorCS"),sQuery(id+"F0.wireOp",EDGE,"E76.26.MirrorCS"),sQuery(id+"F0.wireOp",EDGE,"E76.28.MirrorCS"),sQuery(id+"F0.wireOp",EDGE,"E76.31.MirrorCS"),sQuery(id+"F0.wireOp",EDGE,"E76.35.MirrorCS"),sQuery(id+"F0.wireOp",EDGE,"E76.36.MirrorCS"),sQuery(id+"F0.wireOp",EDGE,"E76.39.MirrorCS"),sQuery(id+"F0.wireOp",EDGE,"E76.40.MirrorCS"),sQuery(id+"F0.wireOp",EDGE,"E76.41.MirrorCS"),sQuery(id+"F0.wireOp",EDGE,"E76.43.MirrorCS"),sQuery(id+"F0.wireOp",EDGE,"E76.44.MirrorCS"),sQuery(id+"F0.wireOp",EDGE,"E76.45.MirrorCS"),sQuery(id+"F0.wireOp",EDGE,"E76.46.MirrorCS"),sQuery(id+"F0.wireOp",EDGE,"E76.48.MirrorCS"),sQuery(id+"F0.wireOp",EDGE,"E76.50.MirrorCS"),sQuery(id+"F0.wireOp",EDGE,"E76.53.MirrorCS"),sQuery(id+"F0.wireOp",EDGE,"E76.54.MirrorCS"),sQuery(id+"F0.wireOp",EDGE,"E76.55.MirrorCS"),sQuery(id+"F0.wireOp",EDGE,"E76.56.MirrorCS"),sQuery(id+"F0.wireOp",EDGE,"E76.61.MirrorCS"),sQuery(id+"F0.wireOp",EDGE,"E76.62.MirrorCS"),sQuery(id+"F0.wireOp",EDGE,"E76.66.MirrorCS"),sQuery(id+"F0.wireOp",EDGE,"E76.67.MirrorCS"),sQuery(id+"F0.wireOp",EDGE,"E76.72.MirrorCS"),sQuery(id+"F0.wireOp",EDGE,"E76.74.MirrorCS"),sQuery(id+"F0.wireOp",EDGE,"E76.77.MirrorCS"),sQuery(id+"F0.wireOp",EDGE,"E76.78.MirrorCS"),sQuery(id+"F0.wireOp",EDGE,"E76.85.MirrorCS"),sQuery(id+"F0.wireOp",EDGE,"E76.90.MirrorCS"),sQuery(id+"F0.wireOp",EDGE,"E76.91.MirrorCS"),sQuery(id+"F0.wireOp",EDGE,"E76.94.MirrorCS")])]});
            hole(context, id + "F3", {"style" : HoleStyle.SIMPLE, "endStyle" : HoleEndStyle.THROUGH, "holeDiameter" : 4.2 * mm, "locations" : qUnion([Q0, Q1]), "scope" : qUnion([Q2]), "isTappedThrough" : true});
        }
    });
